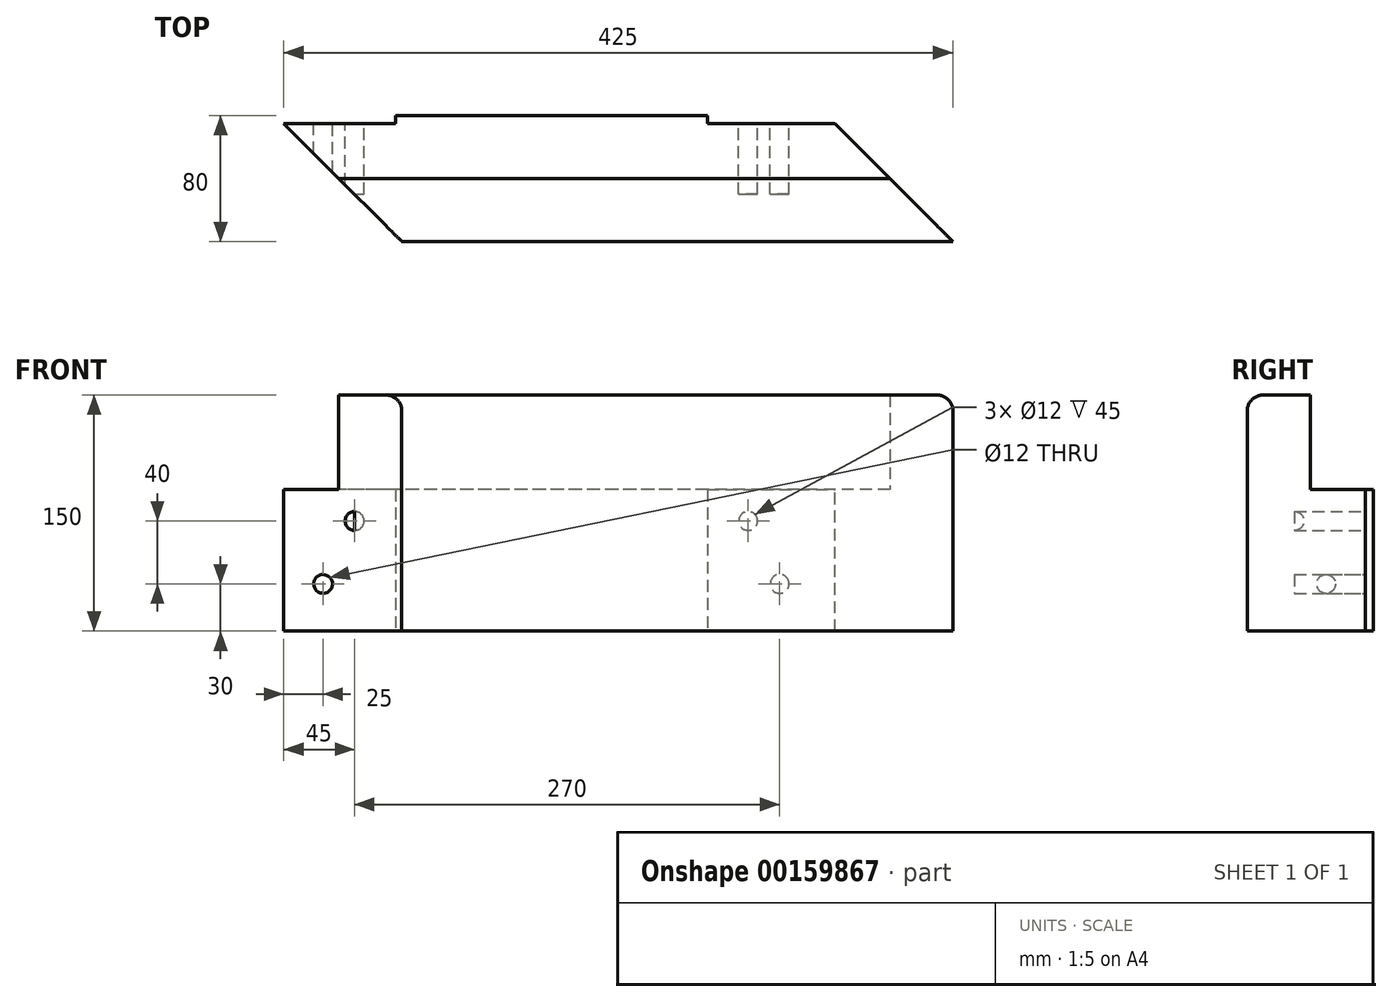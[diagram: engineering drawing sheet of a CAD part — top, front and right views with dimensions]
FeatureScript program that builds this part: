
annotation { "Feature Type Name" : "Feature", "Feature Type Description" : "" }
export const myFeature = defineFeature(function(context is Context, id is Id, definition is map)
    precondition{}
    {
        {
            assignVariable(context, id + "F0", {"name" : "L", "anyValue" : 330 * mm + 100 * mm});
        }
        {
            assignVariable(context, id + "F1", {"name" : "B", "anyValue" : 80 * mm});
        }
        {
            var Q0;
            Q0=qCreatedBy(makeId("Right.planeOp"),FACE);
            var sketch = newSketch(context, id + "F2", { "sketchPlane" : qUnion([Q0])});
            skLineSegment(sketch, "E0.bottom", {"start": v(-40, -75) * mm, "end": v(40, -75) * mm});
            skLineSegment(sketch, "E0.top", {"start": v(-40, 75) * mm, "end": v(0, 75) * mm});
            skLineSegment(sketch, "E0.left", {"start": v(-40, -75) * mm, "end": v(-40, 75) * mm});
            skLineSegment(sketch, "E0.right", {"start": v(40, -75) * mm, "end": v(40, 15) * mm});
            skPoint(sketch, "E0.middle", {"position": v(0, 0) * mm});
            skLineSegment(sketch, "E1", {"start": v(0, 75) * mm, "end": v(0, 15) * mm});
            skLineSegment(sketch, "E2", {"start": v(0, 15) * mm, "end": v(40, 15) * mm});
            skSolve(sketch);
        }
        {
            var Q0;
            Q0=qSketchRegion(id+"F2",true);
            extrude(context, id + "F3", {"entities" : qUnion([Q0]), "endBound" : BoundingType.SYMMETRIC, "depth" : getVariable(context, 'L')});
        }
        {
            var Q0;
            Q0=makeQuery(id+"F3.opExtrude","CAP_EDGE",EDGE,{"disambiguationData":[OSD([sQuery(id+"F2.wireOp",EDGE,"E0.right")])],"isStart":false});
            var Q1;
            Q1=makeQuery(id+"F3.opExtrude","CAP_EDGE",EDGE,{"disambiguationData":[OSD([sQuery(id+"F2.wireOp",EDGE,"E0.left")])],"isStart":true});
            chamfer(context, id + "F4", {"entities" : qUnion([Q0, Q1]), "width" : getVariable(context, 'B'), "tangentPropagation" : true});
        }
        {
            var Q0;
            Q0=makeQuery(id+"F3.opExtrude","SWEPT_FACE",FACE,{"disambiguationData":[OSD([sQuery(id+"F2.wireOp",EDGE,"E0.right")])]});
            var sketch = newSketch(context, id + "F5", { "sketchPlane" : qUnion([Q0])});
            skCircle(sketch, "E3", {"center": v(-105, -45) * mm, "radius": 6 * mm});
            skCircle(sketch, "E4", {"center": v(-85, -5) * mm, "radius": 6 * mm});
            skLineSegment(sketch, "E5", {"start": v(40, 15) * mm, "end": v(40, -75) * mm, "construction": true});
            skCircle(sketch, "E6.MirrorC", {"center": v(165, -5) * mm, "radius": 6 * mm});
            skCircle(sketch, "E7.MirrorC", {"center": v(185, -45) * mm, "radius": 6 * mm});
            skSolve(sketch);
        }
        {
            var Q0;
            Q0=qSketchRegion(id+"F5",true);
            extrude(context, id + "F6", {"entities" : qUnion([Q0]), "operationType" : NewBodyOperationType.REMOVE, "oppositeDirection" : true, "depth" : getVariable(context, 'B') - 30 * mm});
        }
        {
            var Q0;
            Q0=makeQuery(id+"F3.opExtrude","SWEPT_FACE",FACE,{"disambiguationData":[OSD([sQuery(id+"F2.wireOp",EDGE,"E0.right")])]});
            var sketch = newSketch(context, id + "F7", { "sketchPlane" : qUnion([Q0])});
            skLineSegment(sketch, "E8.bottom", {"start": v(-59, 15) * mm, "end": v(-175, 15) * mm});
            skLineSegment(sketch, "E8.top", {"start": v(-59, -75) * mm, "end": v(-175, -75) * mm});
            skLineSegment(sketch, "E8.left", {"start": v(-59, 15) * mm, "end": v(-59, -75) * mm});
            skLineSegment(sketch, "E8.right", {"start": v(-175, 15) * mm, "end": v(-175, -75) * mm});
            skLineSegment(sketch, "E9", {"start": v(40, 15) * mm, "end": v(40, -75) * mm, "construction": true});
            skLineSegment(sketch, "E10.MirrorCS", {"start": v(139, 15) * mm, "end": v(139, -75) * mm});
            skLineSegment(sketch, "E11.MirrorCS", {"start": v(139, 15) * mm, "end": v(255, 15) * mm});
            skLineSegment(sketch, "E12.MirrorCS", {"start": v(139, -75) * mm, "end": v(255, -75) * mm});
            skLineSegment(sketch, "E13.MirrorCS", {"start": v(255, 15) * mm, "end": v(255, -75) * mm});
            skSolve(sketch);
        }
        {
            var Q0;
            Q0=qSketchRegion(id+"F7",true);
            extrude(context, id + "F8", {"entities" : qUnion([Q0]), "operationType" : NewBodyOperationType.REMOVE, "oppositeDirection" : true, "depth" : 5 * mm});
        }
        {
            var Q0;
            Q0=makeQuery(id+"F3.opExtrude","SWEPT_EDGE",EDGE,{"disambiguationData":[OSD([sQuery(id+"F2.wireOp",EDGE,"E0.top"),sQuery(id+"F2.wireOp",EDGE,"E0.left")])]});
            fillet(context, id + "F9", {"entities" : qUnion([Q0]), "radius" : 10 * mm, "tangentPropagation" : true, "allowEdgeOverflow" : false});
        }
    });
